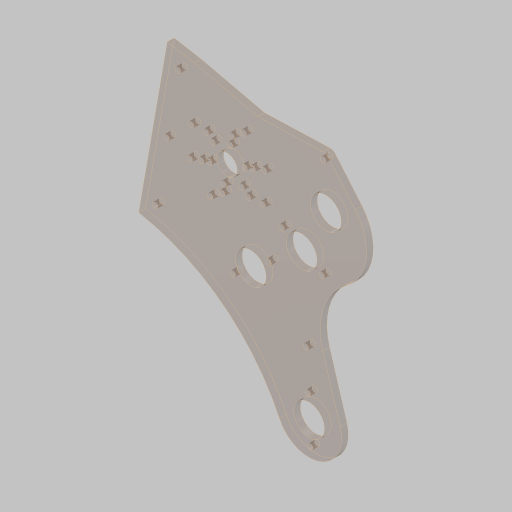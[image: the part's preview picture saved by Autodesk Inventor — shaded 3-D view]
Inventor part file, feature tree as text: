
AUTODESK INVENTOR PART (.ipt)
format: ipt  version: 2023.5 (Build 275446000, 446)  size: 325,632 bytes
history: native  units: in
note: dims shown in document units (in); Inventor stores cm internally (conversion verified against a paired STEP export)
features: sketch x4, hole x3, extrude x2, projected_geometry x2
ambient origin geometry x8: Origin, YZ Plane, XZ Plane, XY Plane, X Axis, Y Axis, Z Axis, Center Point
bodies: Solid1 (feature_tree)
feature tree (11):
  sketch  "Sketch1"  dims[d3=45.0deg d4=0.0in]
  extrude  "Extrusion1"  TaperAngle=0.0deg  [1 undecoded]
  hole  "Hole1"  [1 undecoded]
  hole  "Hole2"  [1 undecoded]
  extrude  "Extrusion2"  Depth=1.75in
  hole  "Hole3"  [1 undecoded]
  sketch  "Sketch2"  dims[d7=4.0in d8=4.0in]
  projected_geometry  "Projected Loop1"
  sketch  "Sketch3"  dims[d9=1.123in d10=4.0in]
  projected_geometry  "Projected Loop2"
  sketch  "Sketch4"  dims[d11=4.5in d12=4.5in d13=0.625in d14=0.625in d15=5.181in d16=1.128in d17=5.181in d18=1.8765in d19=1.8765in d22=1.0in d23=6.0in d26=10.5532in d27=2.5in d30=8.0in d31=0.0687in d32=0.75in d33=4.75in d34=1.375in d35=0.75in d36=0.25in d38=2.3622in d40=360.0deg d44=0.375in d45=0.25in d46=0.0in d47=0.201in d48=0.75in d49=0.37in d50=0.25in d51=90.0deg d52=1.0in d53=0.8108in d55=0.5497in d56=0.3in d57=0.25in d58=2.256in d59=2.5in d60=2.9555in d61=2.35in d62=0.3779in d65=2.0in d66=2.3622in d68=360.0deg d70=1.625in d71=60.0deg d72=1.655in d73=0.201in d74=0.75in d75=0.385in d76=0.25in d77=0.5635in d78=1.0in d79=0.8108in d80=1.5748in d82=360.0deg d85=1.5748in d87=360.0deg d89=45.0deg d90=4.0in d91=1.125in d92=0.625in d93=5.181in d94=0.0in d95=5.5in d96=8.0in d99=0.3126in d100=15.9834in d101=4.0in d102=0.375in d103=5.75in d104=0.375in d105=1.64in d106=1.64in d108=1.6875in d109=0.375in d110=1.4304in d111=0.5in d112=15.0deg d113=1.0in d114=0.0in d115=0.201in d116=0.75in d117=0.385in d118=0.25in d119=0.5635in d120=1.0in d121=0.8108in d122=1.75in d123=0.875in]
note: 4 required parameter values undecoded (feature->parameter linkage not recoverable at this tier; creation-order binding heuristic only, values carry confidence <= 0.55)
